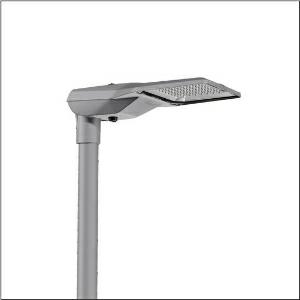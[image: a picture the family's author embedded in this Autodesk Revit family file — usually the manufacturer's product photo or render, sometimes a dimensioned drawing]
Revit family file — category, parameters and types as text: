
# Revit family: streetlight_sl_21_midi___p0_8a_5xe3u33t08nb_6486
name_source: partatom
category: Lighting Fixtures
units: mm (PartAtom-declared; Revit-internal decimal feet)

## family parameters
Cut with Voids When Loaded = No
Host = Face
Light Source = No
Part Type = Normal
Room Calculation Point = No
Round Connector Dimension = Use Diameter
Shared = No

## types (1)
- --- (1 x LED, 22900 lm, 151.2 W, 3000K)
    Apparent Load = 151 VA
    CIE Flux Codes = 36 69 97 100 100
    Color Rendering = 70
    Color Temperature = 3000K
    Default Elevation = 1800 mm
    Description = Streetlight SL 21 midi, mast luminaire, primary light control with lens, of PMMA, primary optical cover: cover, of toughened safety glass, transparent, light distribution: P0.8a, light emission: direct distribution, primary light characteristic: asymmetric, installation type: post-top, side-entry, LED, High Power LED, rated luminous flux: 22.900lm, luminous efficacy: 152lm/W, light colour: 730, colour temperature: 3000K, control gear: D4i, control: pre-setting: logarithmic dimming characteristic, flexible luminous flux parameterisation, time-dependent luminous flux control, constant luminous flux control, overheat protection, mains connection: 230..240V, AC, 50/60Hz, start of lifetime: 151W, end of service life: 157W, reduction: 70W, luminaire housing, of diecast aluminium, powder-coated, Siteco® metallic grey (DB 702S), corrosivity category C5 mid according to DIN EN ISO 12944, multi-level sealing system, sealing non-destructively replaceable, inclination adjustable: 0°, 5°, 10°, 15°, please order mast flange separately, length: 644mm, width: 335mm, height: 110mm, mast flange for spigot size: 42mm (side-entry): 5XC10008XM4, 60/48mm (side-entry/post-top): 5XC10108XM2, 76/60mm (side-entry/post-top): 5XC10108XM1, mounting height: 4..8m, Smart Interface below and above, protection rating (complete): IP66, insulation class (complete): insulation class II (safety insulation), certification: CE, ENEC, ENEC+, VDE, impact resistance: IK10, permissible operating ambient temperature for outdoor applications: -40..+50°C, standard-compliant lighting for roads and squares, packaging unit: 1 piece

Light Distribution: P0.8a
    Height = 111 mm
    Lamp = 1 x LED
    Lamp Light Flux = 22900 lm
    Lamp Power = 151.2 W
    Lamp count = 1
    Length = 644 mm
    Luminous efficacy = 151 lm/W
    Manufacturer = Siteco
    ModVariant = No
    Model = 5XE3U33T08NB
    Number of Poles = 1
    OnlyDefault = Yes
    Power Factor = 1
    Product Name = Streetlight SL 21 midi | P0.8a
    Product group = mast luminaire | pylon top
    ProductGroupID = 6100
    Protection Class = Protection class II
    Protection Degree = IP 66
    RLX_Detail_Level = 1
    RLX_Emergency_Light_Flux = 0 lm
    RLX_Emergency_Type = 0
    RLX_Emergency_Type_DB = No
    RlxData = <blob elided: 26869 chars, md5=f4f1a969>
    Socket = socket
    Standby Power = 0 W
    System Light Flux = 22901 lm
    System Power = 151 W
    Type Comments = factory setting: luminous flux: 100 % | dim-lin: 254 | 802 mA
    Type Image = l_1004304.jpg
    URL = http://relux.com
    VarID = @adj_071402
    Voltage = 0 V
    Weight = 0.00 kg
    Width = 336 mm

## geometry (parser evidence)
native form markers: Blend x4, Sweep x11
no freeform markers — native parametric forms only
